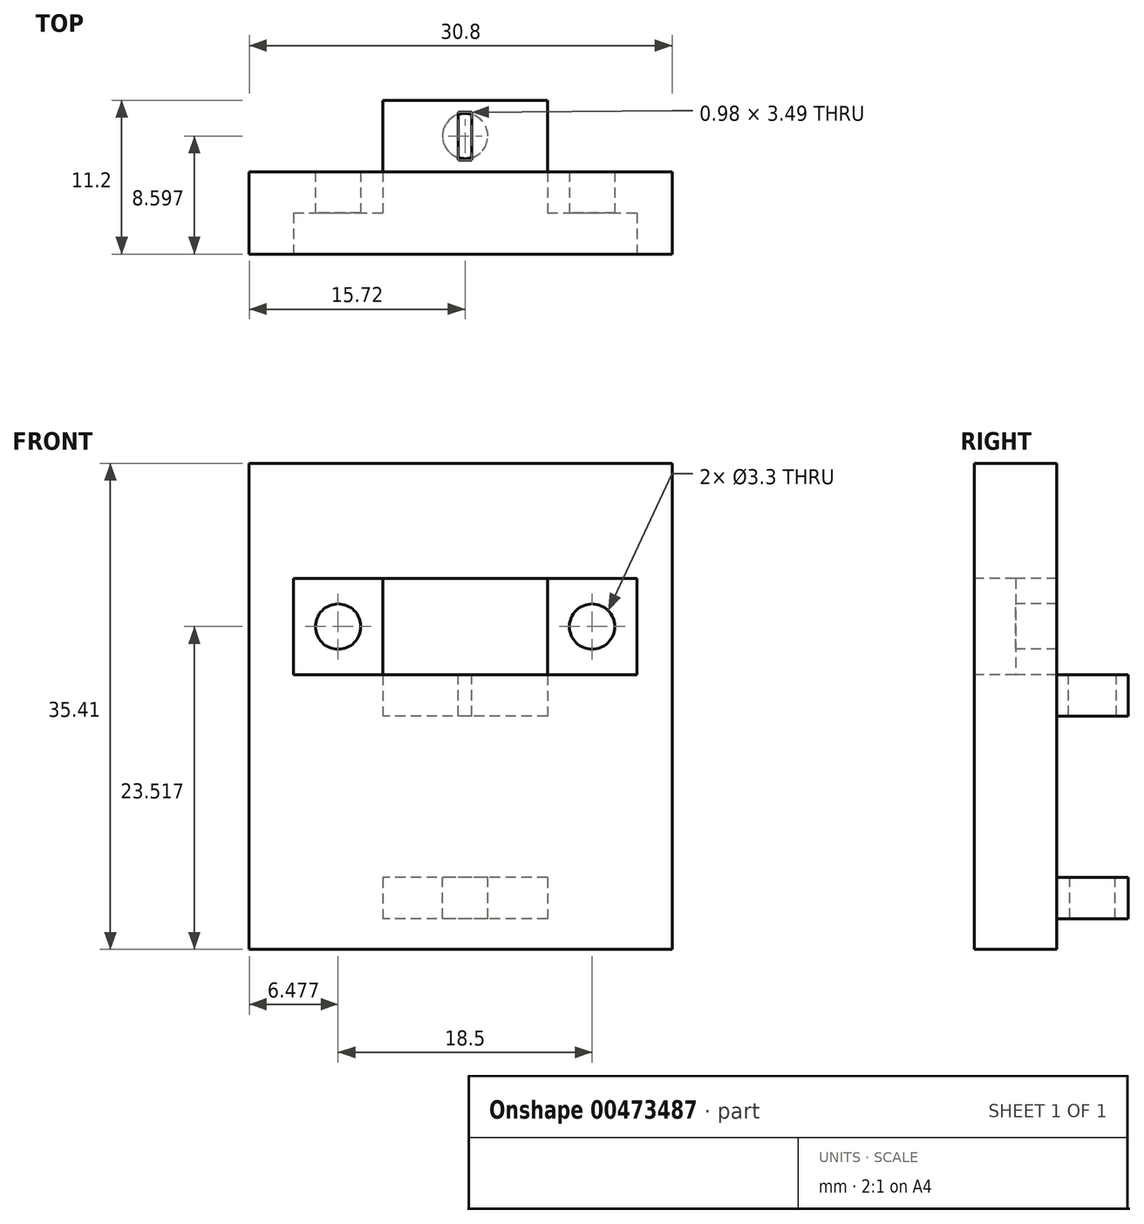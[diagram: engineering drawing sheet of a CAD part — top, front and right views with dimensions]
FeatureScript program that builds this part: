
annotation { "Feature Type Name" : "Feature", "Feature Type Description" : "" }
export const myFeature = defineFeature(function(context is Context, id is Id, definition is map)
    precondition{}
    {
        {
            var Q0;
            Q0=qCreatedBy(makeId("Front.planeOp"),FACE);
            var sketch = newSketch(context, id + "F0", { "sketchPlane" : qUnion([Q0])});
            skLineSegment(sketch, "E0.bottom", {"start": v(-6, 17.16) * mm, "end": v(6, 17.16) * mm});
            skLineSegment(sketch, "E0.top", {"start": v(-6, 10.16) * mm, "end": v(6, 10.16) * mm});
            skLineSegment(sketch, "E0.left", {"start": v(-6, 17.16) * mm, "end": v(-6, 10.16) * mm});
            skLineSegment(sketch, "E0.right", {"start": v(6, 17.16) * mm, "end": v(6, 10.16) * mm});
            skLineSegment(sketch, "E1", {"start": v(-9.24, 13.66) * mm, "end": v(9.26, 13.66) * mm, "construction": true});
            skPoint(sketch, "E1.startSnap0", {"position": v(-6, 13.66) * mm});
            skPoint(sketch, "E1.endSnap0", {"position": v(6, 13.66) * mm});
            skPoint(sketch, "E2", {"position": v(0, 13.66) * mm});
            skLineSegment(sketch, "E3", {"start": v(0, 17.16) * mm, "end": v(0, 10.16) * mm, "construction": true});
            skLineSegment(sketch, "E4.bottom", {"start": v(-15.72, 25.55) * mm, "end": v(15.08, 25.55) * mm});
            skLineSegment(sketch, "E4.top", {"start": v(-15.72, -9.86) * mm, "end": v(15.08, -9.86) * mm});
            skLineSegment(sketch, "E4.left", {"start": v(-15.72, 25.55) * mm, "end": v(-15.72, -9.86) * mm});
            skLineSegment(sketch, "E4.right", {"start": v(15.08, 25.55) * mm, "end": v(15.08, -9.86) * mm});
            skLineSegment(sketch, "E5.bottom", {"start": v(-12.5, 17.16) * mm, "end": v(12.5, 17.16) * mm});
            skLineSegment(sketch, "E5.top", {"start": v(-12.5, 10.16) * mm, "end": v(12.5, 10.16) * mm});
            skLineSegment(sketch, "E5.left", {"start": v(-12.5, 17.16) * mm, "end": v(-12.5, 10.16) * mm});
            skLineSegment(sketch, "E5.right", {"start": v(12.5, 17.16) * mm, "end": v(12.5, 10.16) * mm});
            skSolve(sketch);
        }
        {
            var Q0;
            Q0=makeQuery(id+"F0.imprint","IMPRINT",FACE,{"disambiguationData":[TD([[makeQuery(id+"F0.imprint","IMPRINT",EDGE,{"derivedFrom":sQuery(id+"F0.wireOp",EDGE,"E4.bottom")}),-1.0]])]});
            var Q1;
            {var subQ0=sQuery(id+"F0.wireOp",EDGE,"E0.left");Q1=makeQuery(id+"F0.imprint","IMPRINT",FACE,{"disambiguationData":[TD([[makeQuery(id+"F0.imprint","IMPRINT",EDGE,{"derivedFrom":subQ0}),-1.0]])]});}
            var Q2;
            {var subQ0=sQuery(id+"F0.wireOp",EDGE,"E0.right");Q2=makeQuery(id+"F0.imprint","IMPRINT",FACE,{"disambiguationData":[TD([[makeQuery(id+"F0.imprint","IMPRINT",EDGE,{"derivedFrom":subQ0}),1.0]])]});}
            extrude(context, id + "F1", {"entities" : qUnion([Q0, Q1, Q2]), "oppositeDirection" : true, "depth" : 6 * mm});
        }
        {
            var Q0;
            {var subQ0=sQuery(id+"F0.wireOp",EDGE,"E0.left");Q0=makeQuery(id+"F0.imprint","IMPRINT",FACE,{"disambiguationData":[TD([[makeQuery(id+"F0.imprint","IMPRINT",EDGE,{"derivedFrom":subQ0}),-1.0]])]});}
            var Q1;
            {var subQ0=sQuery(id+"F0.wireOp",EDGE,"E0.right");Q1=makeQuery(id+"F0.imprint","IMPRINT",FACE,{"disambiguationData":[TD([[makeQuery(id+"F0.imprint","IMPRINT",EDGE,{"derivedFrom":subQ0}),1.0]])]});}
            extrude(context, id + "F2", {"entities" : qUnion([Q0, Q1]), "operationType" : NewBodyOperationType.REMOVE, "oppositeDirection" : true, "depth" : 3 * mm});
        }
        {
            var Q0;
            Q0=sQuery(id+"F0.wireOp",VERTEX,"E1.start");
            var Q1;
            Q1=sQuery(id+"F0.wireOp",VERTEX,"E1.end");
            var Q2;
            Q2=makeQuery(id+"F1.opExtrude","SWEPT_BODY",BODY,{"disambiguationData":[OSD([sQuery(id+"F0.wireOp",EDGE,"E0.left"),sQuery(id+"F0.wireOp",EDGE,"E0.right"),sQuery(id+"F0.wireOp",EDGE,"E4.bottom"),sQuery(id+"F0.wireOp",EDGE,"E4.top"),sQuery(id+"F0.wireOp",EDGE,"E4.left"),sQuery(id+"F0.wireOp",EDGE,"E4.right"),sQuery(id+"F0.wireOp",EDGE,"E5.bottom"),sQuery(id+"F0.wireOp",EDGE,"E5.top")])]});
            hole(context, id + "F3", {"style" : HoleStyle.SIMPLE, "endStyle" : HoleEndStyle.THROUGH, "standardTappedOrClearance" : lookupTablePath({ "standard" : "ISO", "fit" : "Normal", "size" : "M3", "type" : "Clearance" }), "standardBlindInLast" : lookupTablePath({ "fit" : "Standard", "standard" : "ISO", "size" : "M3", "type" : "Clearance" }), "holeDiameter" : 3.3 * mm, "isTappedThrough" : true, "tappedDepth" : 12 * mm, "tapClearance" : 3, "locations" : qUnion([Q0, Q1]), "scope" : qUnion([Q2])});
        }
        {
            var Q0;
            Q0=makeQuery(id+"F1.opExtrude","CAP_FACE",FACE,{"disambiguationData":[OSD([sQuery(id+"F0.wireOp",EDGE,"E0.left"),sQuery(id+"F0.wireOp",EDGE,"E0.right"),sQuery(id+"F0.wireOp",EDGE,"E4.bottom"),sQuery(id+"F0.wireOp",EDGE,"E4.top"),sQuery(id+"F0.wireOp",EDGE,"E4.left"),sQuery(id+"F0.wireOp",EDGE,"E4.right"),sQuery(id+"F0.wireOp",EDGE,"E5.bottom"),sQuery(id+"F0.wireOp",EDGE,"E5.top")])],"isStart":false});
            var sketch = newSketch(context, id + "F4", { "sketchPlane" : qUnion([Q0])});
            skLineSegment(sketch, "E6.bottom", {"start": v(-6, -4.63) * mm, "end": v(6, -4.63) * mm});
            skLineSegment(sketch, "E6.top", {"start": v(-6, -7.63) * mm, "end": v(6, -7.63) * mm});
            skLineSegment(sketch, "E6.left", {"start": v(-6, -4.63) * mm, "end": v(-6, -7.63) * mm});
            skLineSegment(sketch, "E6.right", {"start": v(6, -4.63) * mm, "end": v(6, -7.63) * mm});
            skLineSegment(sketch, "E7.bottom", {"start": v(-6, 10.14) * mm, "end": v(6, 10.14) * mm});
            skLineSegment(sketch, "E7.top", {"start": v(-6, 7.14) * mm, "end": v(6, 7.14) * mm});
            skLineSegment(sketch, "E7.left", {"start": v(-6, 10.14) * mm, "end": v(-6, 7.14) * mm});
            skLineSegment(sketch, "E7.right", {"start": v(6, 10.14) * mm, "end": v(6, 7.14) * mm});
            skLineSegment(sketch, "E8.left", {"start": v(-6, 10.16) * mm, "end": v(-6, -7.63) * mm, "construction": true});
            skLineSegment(sketch, "E8.right", {"start": v(6, 10.16) * mm, "end": v(6, -7.63) * mm, "construction": true});
            skSolve(sketch);
        }
        {
            var Q0;
            Q0=makeQuery(id+"F4.imprint","IMPRINT",FACE,{"disambiguationData":[TD([[makeQuery(id+"F4.imprint","IMPRINT",EDGE,{"derivedFrom":sQuery(id+"F4.wireOp",EDGE,"E6.bottom")}),-1.0]])]});
            var Q1;
            Q1=makeQuery(id+"F4.imprint","IMPRINT",FACE,{"disambiguationData":[TD([[makeQuery(id+"F4.imprint","IMPRINT",EDGE,{"derivedFrom":sQuery(id+"F4.wireOp",EDGE,"E7.bottom")}),-1.0]])]});
            extrude(context, id + "F5", {"entities" : qUnion([Q0, Q1]), "operationType" : NewBodyOperationType.ADD, "depth" : 5.2 * mm});
        }
        {
            var Q0;
            Q0=makeQuery(id+"F5.opExtrude","SWEPT_FACE",FACE,{"disambiguationData":[OSD([sQuery(id+"F4.wireOp",EDGE,"E7.bottom")])]});
            var sketch = newSketch(context, id + "F6", { "sketchPlane" : qUnion([Q0])});
            skLineSegment(sketch, "E9", {"start": v(-6, 6) * mm, "end": v(6, 11.2) * mm, "construction": true});
            skPoint(sketch, "E10", {"position": v(0, 8.6) * mm});
            skLineSegment(sketch, "E11.bottom", {"start": v(-0.49, 10.34) * mm, "end": v(0.49, 10.34) * mm});
            skLineSegment(sketch, "E11.top", {"start": v(-0.49, 6.85) * mm, "end": v(0.49, 6.85) * mm});
            skLineSegment(sketch, "E11.left", {"start": v(-0.49, 10.34) * mm, "end": v(-0.49, 6.85) * mm});
            skLineSegment(sketch, "E11.right", {"start": v(0.49, 10.34) * mm, "end": v(0.49, 6.85) * mm});
            skSolve(sketch);
        }
        {
            var Q0;
            Q0 = qSketchRegion(id + "F6", true);
            extrude(context, id + "F7", {"entities" : qUnion([Q0]), "operationType" : NewBodyOperationType.REMOVE, "endBound" : BoundingType.UP_TO_NEXT, "oppositeDirection" : true, "depth" : 25 * mm});
        }
        {
            var Q0;
            Q0=makeQuery(id+"F5.opExtrude","SWEPT_FACE",FACE,{"disambiguationData":[OSD([sQuery(id+"F4.wireOp",EDGE,"E6.bottom")])]});
            var sketch = newSketch(context, id + "F8", { "sketchPlane" : qUnion([Q0])});
            skLineSegment(sketch, "E12", {"start": v(-6, 6) * mm, "end": v(6, 11.2) * mm, "construction": true});
            skPoint(sketch, "E13", {"position": v(0, 8.6) * mm});
            skSolve(sketch);
        }
        {
            var Q0;
            Q0=sQuery(id+"F8.wireOp",VERTEX,"E13");
            var Q1;
            Q1=makeQuery(id+"F1.opExtrude","SWEPT_BODY",BODY,{"disambiguationData":[OSD([sQuery(id+"F0.wireOp",EDGE,"E0.left"),sQuery(id+"F0.wireOp",EDGE,"E0.right"),sQuery(id+"F0.wireOp",EDGE,"E4.bottom"),sQuery(id+"F0.wireOp",EDGE,"E4.top"),sQuery(id+"F0.wireOp",EDGE,"E4.left"),sQuery(id+"F0.wireOp",EDGE,"E4.right"),sQuery(id+"F0.wireOp",EDGE,"E5.bottom"),sQuery(id+"F0.wireOp",EDGE,"E5.top")])]});
            hole(context, id + "F9", {"style" : HoleStyle.SIMPLE, "endStyle" : HoleEndStyle.THROUGH, "standardTappedOrClearance" : lookupTablePath({ "standard" : "ISO", "fit" : "Normal", "size" : "M3", "type" : "Clearance" }), "standardBlindInLast" : lookupTablePath({ "fit" : "Standard", "standard" : "ISO", "size" : "M3", "type" : "Clearance" }), "holeDiameter" : 3.3 * mm, "isTappedThrough" : true, "tappedDepth" : 12 * mm, "tapClearance" : 3, "locations" : qUnion([Q0]), "scope" : qUnion([Q1])});
        }
    });
